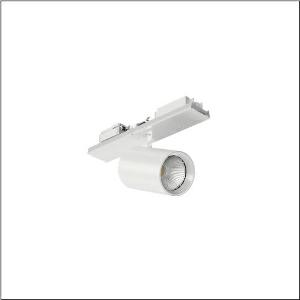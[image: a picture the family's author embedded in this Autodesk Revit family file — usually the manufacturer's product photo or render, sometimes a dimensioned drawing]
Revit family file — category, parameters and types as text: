
# Revit family: licross_r__spot_31_51sl147a43b_2678
name_source: partatom
category: Lighting Fixtures
units: mm (PartAtom-declared; Revit-internal decimal feet)

## family parameters
Cut with Voids When Loaded = No
Host = Face
Light Source = No
Part Type = Normal
Room Calculation Point = No
Round Connector Dimension = Use Diameter
Shared = No

## types (1)
- --- (1 x LED, 3720 lm, 27.9 W, 4000K)
    Apparent Load = 28 VA
    CIE Flux Codes = 93 97 100 100 100
    Color Rendering = 90
    Color Temperature = 4000K
    Default Elevation = 1800 mm
    Description = Licross® Spot 31, directional spotlight, light control with lens, of plastic, LED rated luminous flux: 3.720lm, light colour: 940, with plug, 3-pole, with phase selection, mains connection: 220..240V, AC, 50/60Hz, of aluminium, traffic white (RAL 9016), length: 140mm, diameter: 90mm, protection rating (complete): IP20, insulation class (complete): insulation class I (protective earthing), certification: CE, packaging unit: 1 piece
    Height = 175 mm
    Lamp = 1 x LED
    Lamp Light Flux = 3720 lm
    Lamp Power = 27.9 W
    Lamp count = 1
    Length = 90 mm
    Luminous efficacy = 133 lm/W
    Manufacturer = Siteco
    ModVariant = No
    Model = 51SL147A43B
    Mounting Place = Ceiling
    Mounting Type = Pendant
    Number of Poles = 1
    OnlyDefault = Yes
    Power Factor = 1
    Product Name = Licross® Spot 31
    Product group = directional spotlight
    ProductGroupID = 905
    Protection Class = Protection class I
    Protection Degree = IP 20
    RLX_Detail_Level = 1
    RLX_Emergency_Light_Flux = 0 lm
    RLX_Emergency_Type = 0
    RLX_Emergency_Type_DB = No
    RlxData = <blob elided: 14849 chars, md5=b6f611ac>
    Socket = socket
    Standby Power = 0 W
    System Light Flux = 3720 lm
    System Power = 28 W
    Type Comments = factory setting: luminous flux: 100 % | (ON | ON | ON) | 700 mA
    Type Image = l_1245720.jpg
    URL = http://relux.com
    VarID = @adj_081779
    Voltage = 0 V
    Weight = 0.00 kg
    Width = 0 mm  [stored 0 ft]

note: [stored X ft] marks values corroborated as IEEE doubles in the binary element streams (Revit-internal decimal feet)

## geometry (parser evidence)
native form markers: Sweep x10
no freeform markers — native parametric forms only
